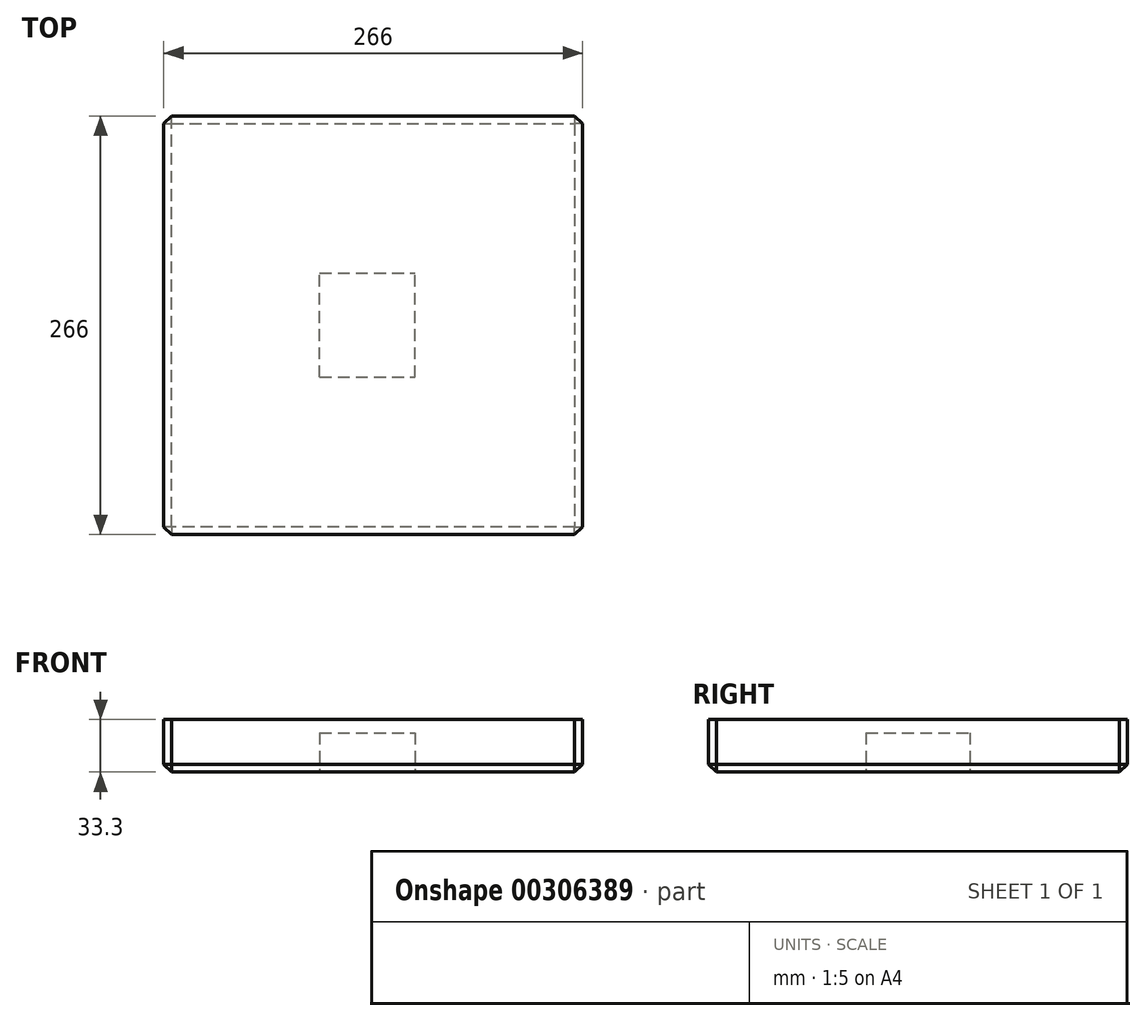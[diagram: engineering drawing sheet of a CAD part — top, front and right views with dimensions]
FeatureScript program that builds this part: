
annotation { "Feature Type Name" : "Feature", "Feature Type Description" : "" }
export const myFeature = defineFeature(function(context is Context, id is Id, definition is map)
    precondition{}
    {
        {
            var Q0;
            Q0=qCreatedBy(makeId("Front.planeOp"),FACE);
            var sketch = newSketch(context, id + "F0", { "sketchPlane" : qUnion([Q0])});
            skLineSegment(sketch, "E0.bottom", {"start": v(-129.36, 33.3) * mm, "end": v(136.64, 33.3) * mm});
            skLineSegment(sketch, "E0.top", {"start": v(-129.36, 0) * mm, "end": v(136.64, 0) * mm});
            skLineSegment(sketch, "E0.left", {"start": v(-129.36, 33.3) * mm, "end": v(-129.36, 0) * mm});
            skLineSegment(sketch, "E0.right", {"start": v(136.64, 33.3) * mm, "end": v(136.64, 0) * mm});
            skSolve(sketch);
        }
        {
            var Q0;
            Q0=makeQuery(id+"F0.imprint","IMPRINT",FACE,{"disambiguationData":[TD([[makeQuery(id+"F0.imprint","IMPRINT",EDGE,{"derivedFrom":sQuery(id+"F0.wireOp",EDGE,"E0.bottom")}),-1.0]])]});
            extrude(context, id + "F1", {"entities" : qUnion([Q0]), "depth" : 266 * mm});
        }
        {
            var Q0;
            Q0=makeQuery(id+"F1.opExtrude","SWEPT_FACE",FACE,{"disambiguationData":[OSD([sQuery(id+"F0.wireOp",EDGE,"E0.top")])]});
            var sketch = newSketch(context, id + "F2", { "sketchPlane" : qUnion([Q0])});
            skLineSegment(sketch, "E1.bottom", {"start": v(-30.27, 166) * mm, "end": v(30.27, 166) * mm});
            skLineSegment(sketch, "E1.top", {"start": v(-30.27, 100) * mm, "end": v(30.27, 100) * mm});
            skLineSegment(sketch, "E1.left", {"start": v(-30.27, 166) * mm, "end": v(-30.27, 100) * mm});
            skLineSegment(sketch, "E1.right", {"start": v(30.27, 166) * mm, "end": v(30.27, 100) * mm});
            skPoint(sketch, "E1.middle", {"position": v(0, 133) * mm});
            skPoint(sketch, "E1.middle.positionSnap0", {"position": v(-129.36, 133) * mm});
            skPoint(sketch, "E1.centerSnap0", {"position": v(-129.36, 133) * mm});
            skSolve(sketch);
        }
        {
            var Q0;
            Q0=makeQuery(id+"F2.imprint","IMPRINT",FACE,{"disambiguationData":[TD([[makeQuery(id+"F2.imprint","IMPRINT",EDGE,{"derivedFrom":sQuery(id+"F2.wireOp",EDGE,"E1.bottom")}),-1.0]])]});
            extrude(context, id + "F3", {"entities" : qUnion([Q0]), "operationType" : NewBodyOperationType.REMOVE, "oppositeDirection" : true, "depth" : 25 * mm});
        }
        {
            var Q0;
            Q0=makeQuery(id+"F1.opExtrude","CAP_EDGE",EDGE,{"disambiguationData":[OSD([sQuery(id+"F0.wireOp",EDGE,"E0.right")])],"isStart":false});
            var Q1;
            Q1=makeQuery(id+"F1.opExtrude","CAP_EDGE",EDGE,{"disambiguationData":[OSD([sQuery(id+"F0.wireOp",EDGE,"E0.right")])],"isStart":true});
            var Q2;
            Q2=makeQuery(id+"F1.opExtrude","CAP_EDGE",EDGE,{"disambiguationData":[OSD([sQuery(id+"F0.wireOp",EDGE,"E0.left")])],"isStart":true});
            var Q3;
            Q3=makeQuery(id+"F1.opExtrude","CAP_EDGE",EDGE,{"disambiguationData":[OSD([sQuery(id+"F0.wireOp",EDGE,"E0.left")])],"isStart":false});
            var Q4;
            Q4=makeQuery(id+"F1.opExtrude","SWEPT_EDGE",EDGE,{"disambiguationData":[OSD([sQuery(id+"F0.wireOp",EDGE,"E0.top"),sQuery(id+"F0.wireOp",EDGE,"E0.left")])]});
            var Q5;
            Q5=makeQuery(id+"F1.opExtrude","CAP_EDGE",EDGE,{"disambiguationData":[OSD([sQuery(id+"F0.wireOp",EDGE,"E0.top")])],"isStart":false});
            var Q6;
            Q6=makeQuery(id+"F1.opExtrude","SWEPT_EDGE",EDGE,{"disambiguationData":[OSD([sQuery(id+"F0.wireOp",EDGE,"E0.top"),sQuery(id+"F0.wireOp",EDGE,"E0.right")])]});
            var Q7;
            Q7=makeQuery(id+"F1.opExtrude","CAP_EDGE",EDGE,{"disambiguationData":[OSD([sQuery(id+"F0.wireOp",EDGE,"E0.top")])],"isStart":true});
            chamfer(context, id + "F4", {"entities" : qUnion([Q0, Q1, Q2, Q3, Q4, Q5, Q6, Q7]), "width" : 5 * mm, "tangentPropagation" : true});
        }
    });
